# Revit family: Tub_And_Shower_Unit-Zurn
name_source: partatom
category: Plumbing Fixtures
revit_build: Autodesk Revit Architecture 2015 (Build: 20140606_1530(x64)
units: mm (PartAtom-declared; Revit-internal decimal feet)

## types (1)
- Z7500-DV-HW
    Aqua Panel On = Yes
    Assembly Code = C1030210
    CTRL Face Position = 0' - 2 1/2"
    Description = Aqua-Panel Shower Unit
    Diverter Placement Height = 1' - 4"
    Diverter Visibility = Yes
    Flow Control Placement Height = 0' - 8"
    Flow Control Visibility = Yes
    Handset Offset From Center = 0' - 8"
    Handset Placement Height = 1' - 3 3/4"
    Handset Type = Shower_Hand_Unit-Zurn-Z7300 : Z7300
    Handset Visibility = Yes
    Height = 2' - 8"
    Hose Connection Placement Height = 1' - 9 3/4"
    Hose Height Left = 2' - 6"
    Hose Height Right = 2' - 0 3/16"
    Hose Offset From Center (Left) = 0' - 3 7/8"
    Hose Offset From Center (Right) = 0' - 8"
    Hose Visibility = Yes
    Manufacturer = Zurn Industries, LLC.
    Model = Z7500-DV-HW
    Mounting Bar Glide Height = 0' - 8"
    Mounting Bar Placement Height = 2' - 7"
    Mounting Bar Visibility = Yes
    Product Documentation Link = http://www.zurn.com
    Product data url = https://bimobject.com
    Shower Head Placement Height = 2' - 3 1/2"
    Shower Head Supply Offset (F/B) = 0' - 2 1/8"
    Shower Head Type = Shower_Head-Institutioinal-Zurn-Z7500-i2-Fixed_Spray : 2.5GPM Z7500-i2
    Shower Head Visibility = Yes
    Shower Piping Supply Radius = 0' - 0 3/8"
    Shower Supply Radius = 0' - 0 3/8"
    Soap Dish Visability = Yes
    Spout Distence Below Flow Control = 1' - 0"
    Spout Supply Offset (F/B) = 0' - 1 1/2"
    Spout Visibility = No
    Supply Plumbing Visible = No
    URL = http://www.zurn.com
    Wall Mounted Hose = No

## geometry (parser evidence)
native form markers: Extrusion x1, Revolve x3, Sweep x35
no freeform markers — native parametric forms only
